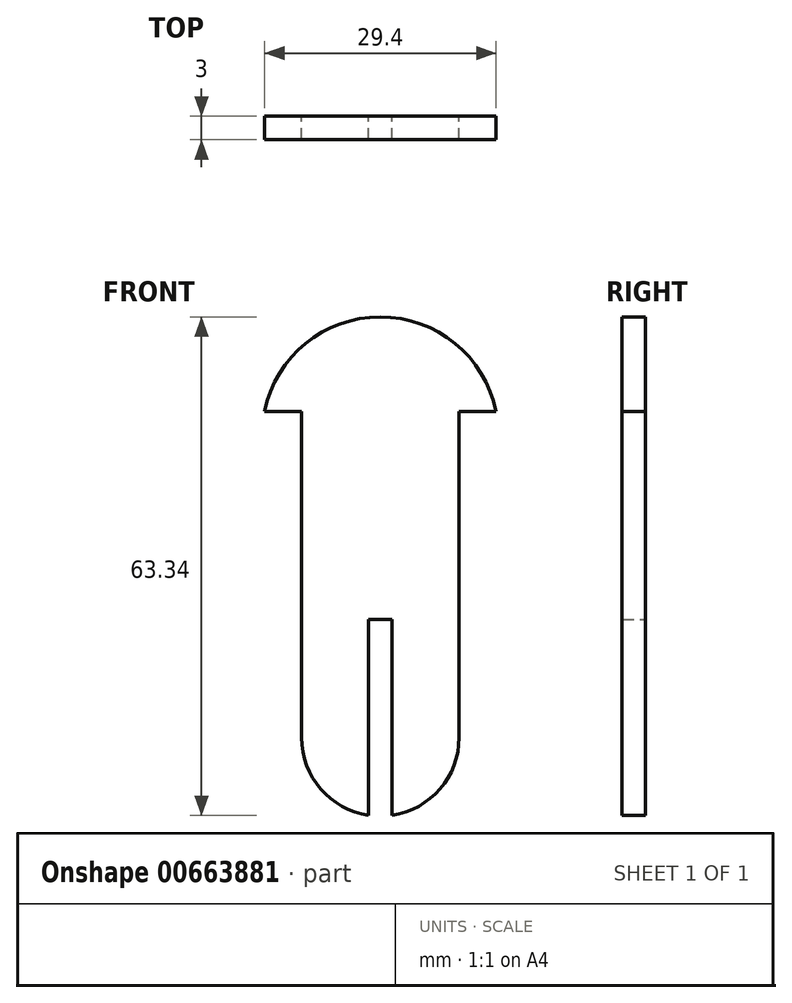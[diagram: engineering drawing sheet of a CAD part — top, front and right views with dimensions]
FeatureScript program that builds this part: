
annotation { "Feature Type Name" : "Feature", "Feature Type Description" : "" }
export const myFeature = defineFeature(function(context is Context, id is Id, definition is map)
    precondition{}
    {
        {
            var Q0;
            Q0=qCreatedBy(makeId("Front.planeOp"),FACE);
            var sketch = newSketch(context, id + "F0", { "sketchPlane" : qUnion([Q0])});
            skLineSegment(sketch, "E0.left", {"start": v(10, 20.73) * mm, "end": v(10, -20.72) * mm});
            skLineSegment(sketch, "E0.right", {"start": v(-10, 20.73) * mm, "end": v(-10, -20.72) * mm});
            skPoint(sketch, "E0.middle", {"position": v(0, 0) * mm});
            skArc(sketch, "E1", {"start": v(14.7, 20.73) * mm, "mid": v(0, 32.73) * mm, "end": v(-14.7, 20.73) * mm});
            skArc(sketch, "E2", {"start": v(-10, -20.73) * mm, "mid": v(-7.58, -27.24) * mm, "end": v(-1.5, -30.61) * mm});
            skLineSegment(sketch, "E3", {"start": v(-14.7, 20.73) * mm, "end": v(-10, 20.73) * mm});
            skLineSegment(sketch, "E4", {"start": v(10, 20.73) * mm, "end": v(14.7, 20.73) * mm});
            skLineSegment(sketch, "E5.bottom", {"start": v(-1.5, -5.72) * mm, "end": v(1.5, -5.72) * mm});
            skLineSegment(sketch, "E5.left", {"start": v(-1.5, -5.72) * mm, "end": v(-1.5, -30.61) * mm});
            skLineSegment(sketch, "E5.right", {"start": v(1.5, -5.72) * mm, "end": v(1.5, -30.61) * mm});
            skArc(sketch, "E6.trimOffspring", {"start": v(1.5, -30.61) * mm, "mid": v(7.58, -27.24) * mm, "end": v(10, -20.72) * mm});
            skSolve(sketch);
        }
        {
            var Q0;
            Q0 = qSketchRegion(id + "F0", true);
            extrude(context, id + "F1", {"entities" : qUnion([Q0]), "depth" : 3 * mm, "offsetDistance" : 25 * mm});
        }
    });
